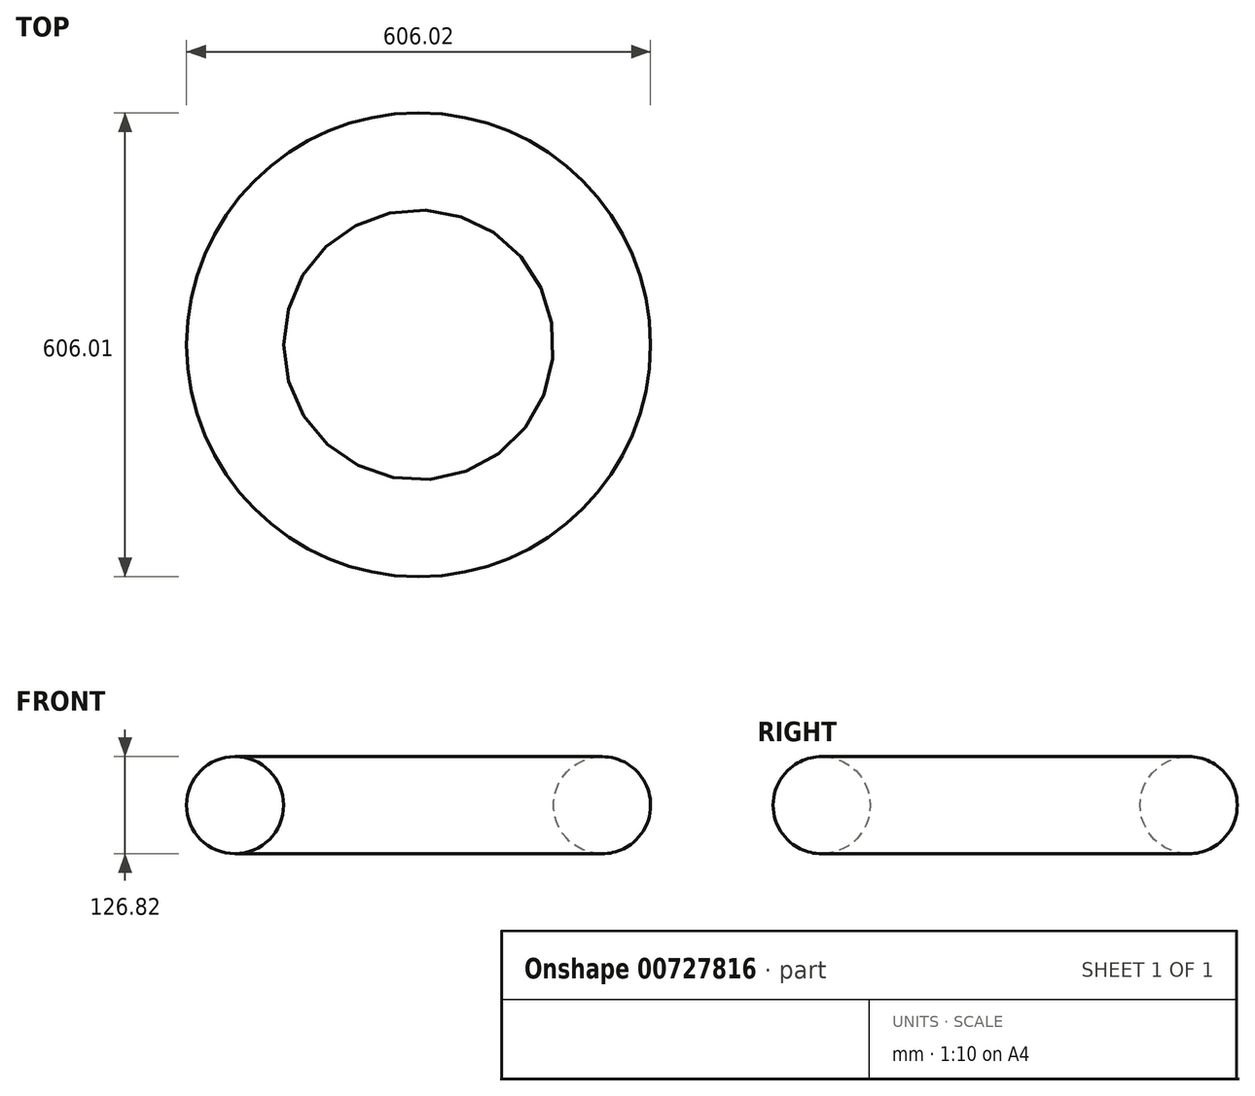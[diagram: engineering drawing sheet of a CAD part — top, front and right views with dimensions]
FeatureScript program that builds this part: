
annotation { "Feature Type Name" : "Feature", "Feature Type Description" : "" }
export const myFeature = defineFeature(function(context is Context, id is Id, definition is map)
    precondition{}
    {
        {
            var Q0;
            Q0=qCreatedBy(makeId("Right.planeOp"),FACE);
            var sketch = newSketch(context, id + "F0", { "sketchPlane" : qUnion([Q0])});
            skCircle(sketch, "E0", {"center": v(-43.32, -46.3) * mm, "radius": 63.4 * mm});
            skLineSegment(sketch, "E1", {"start": v(-282.92, -174.55) * mm, "end": v(-282.92, 156.9) * mm});
            skSolve(sketch);
        }
        {
            var Q0;
            Q0=makeQuery(id+"F0.imprint","IMPRINT",FACE,{"disambiguationData":[TD([[makeQuery(id+"F0.imprint","IMPRINT",EDGE,{"derivedFrom":sQuery(id+"F0.wireOp",EDGE,"E0")}),1.0]])]});
            var Q1;
            Q1=sQuery(id+"F0.wireOp",EDGE,"E1");
            revolve(context, id + "F1", {"surfaceOperationType" : NewSurfaceOperationType.NEW, "entities" : qUnion([Q0]), "axis" : qUnion([Q1]), "revolveType" : RevolveType.FULL});
        }
    });
